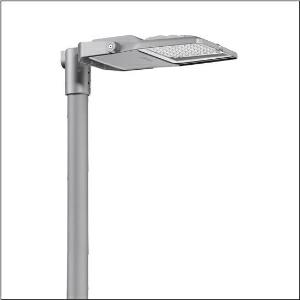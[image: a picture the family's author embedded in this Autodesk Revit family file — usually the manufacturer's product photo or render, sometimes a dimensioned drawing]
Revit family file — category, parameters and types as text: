
# Revit family: floodlight_fl_21_iq_mini___pl64_5xa7772b4e3a_29df
name_source: partatom
category: Lighting Fixtures
units: mm (PartAtom-declared; Revit-internal decimal feet)

## family parameters
Cut with Voids When Loaded = No
Host = Face
Light Source = No
Part Type = Normal
Room Calculation Point = No
Round Connector Dimension = Use Diameter
Shared = No

## types (1)
- --- (1 x LED, 6270 lm, 45.5 W, 4000K)
    Apparent Load = 46 VA
    CIE Flux Codes = 28 80 98 100 100
    Color Rendering = 70
    Color Temperature = 4000K
    Default Elevation = 1800 mm
    Description = Floodlight FL 21 iQ mini, floodlight, primary light control with lens, of PMMA, primary optical cover: protective disc, of toughened safety glass, transparent, light distribution: PL64, light emission: direct distribution, installation type: surface-mounted, LED, High Power LED, rated luminous flux: 6.270lm, luminous efficacy: 138lm/W, light colour: 740, colour temperature: 4000K, control: Auto-Match, Temp-Guard, Night-Set, Smart-Wire, Desk-Remote (wireless, voltage-free reading and setting of iQ features in the workshop via application-optimized NFC function/RFID function), optimised constant luminous flux control (CLO 2.0), Light-Fading, Lumen-Switch, with terminal, 6-pole, mains connection: 220..240V, AC, 50/60Hz, start of lifetime: 46W, end of service life: 48W, reduction: 22W, luminaire housing, of diecast aluminium, powder-coated, Siteco® metallic grey (DB 702S), corrosivity category C5 mid according to DIN EN ISO 12944, sealing non-destructively replaceable, please order mast flange separately, mast bracket, of steel, galvanised, powder-coated, protection rating (complete): IP66, insulation class (complete): insulation class II (safety insulation), certification: CE, ENEC, VDE, protection symbol: D, impact resistance: IK08, permissible operating ambient temperature: -40..+40°C, permissible operating ambient temperature for outdoor applications: -40..+50°C, standard: DIN EN 12944, LABS conformity tested according to VDMA 24364:2018-05, packaging unit: 1 piece

Light Distribution: PL64
    Height = 70 mm
    Lamp = 1 x LED
    Lamp Light Flux = 6270 lm
    Lamp Power = 45.5 W
    Lamp count = 1
    Length = 485 mm
    Luminous efficacy = 138 lm/W
    Manufacturer = Siteco
    ModVariant = No
    Model = 5XA7772B4E3A
    Number of Poles = 1
    OnlyDefault = Yes
    Power Factor = 1
    Product Name = Floodlight FL 21 iQ mini | PL64
    Product group = floodlight | pylon annexe
    ProductGroupID = 6200
    Protection Class = Protection class II
    Protection Degree = IP 66
    RLX_Detail_Level = 1
    RLX_Emergency_Light_Flux = 0 lm
    RLX_Emergency_Type = 0
    RLX_Emergency_Type_DB = No
    RlxData = <blob elided: 101213 chars, md5=ea43227a>
    Socket = socket
    Standby Power = 0 W
    System Light Flux = 6270 lm
    System Power = 46 W
    Type Comments = factory setting: luminous flux: 100 % | dim-lin: 254 | 463 mA
    Type Image = l_1007125.jpg
    URL = http://relux.com
    VarID = @adj_099057
    Voltage = 0 V
    Weight = 0.00 kg
    Width = 337 mm

## geometry (parser evidence)
native form markers: Blend x4, Sweep x13
no freeform markers — native parametric forms only
